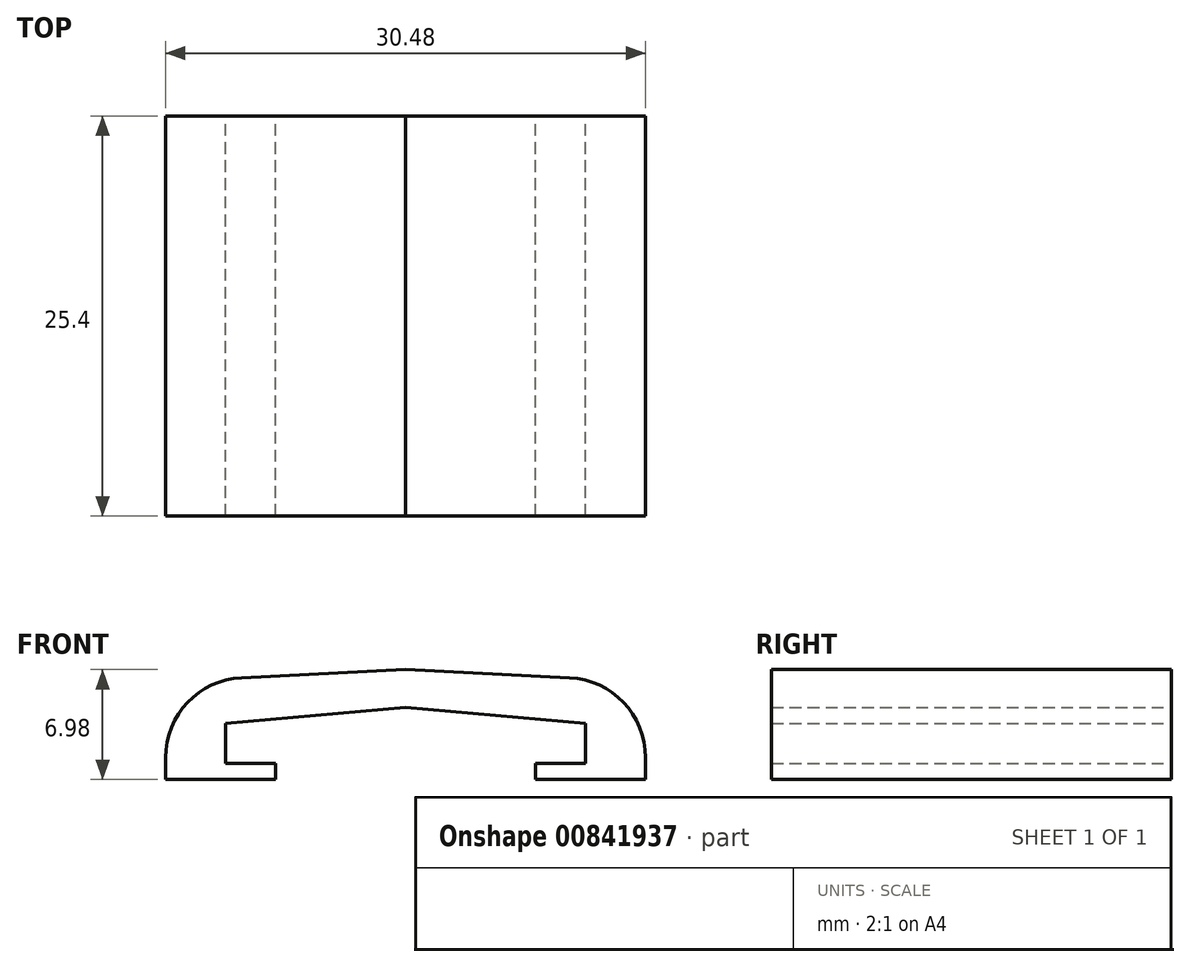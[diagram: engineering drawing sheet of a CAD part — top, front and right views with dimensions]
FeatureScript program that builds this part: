
annotation { "Feature Type Name" : "Feature", "Feature Type Description" : "" }
export const myFeature = defineFeature(function(context is Context, id is Id, definition is map)
    precondition{}
    {
        {
            var Q0;
            Q0=qCreatedBy(makeId("Front.planeOp"),FACE);
            var sketch = newSketch(context, id + "F0", { "sketchPlane" : qUnion([Q0])});
            skLineSegment(sketch, "E0", {"start": v(-11.43, 17.28) * mm, "end": v(11.43, 17.28) * mm, "construction": true});
            skLineSegment(sketch, "E1", {"start": v(-11.43, 17.28) * mm, "end": v(0, 18.28) * mm});
            skLineSegment(sketch, "E2", {"start": v(0, 18.28) * mm, "end": v(11.43, 17.28) * mm});
            skLineSegment(sketch, "E3", {"start": v(-11.43, 17.28) * mm, "end": v(-11.43, 14.74) * mm});
            skLineSegment(sketch, "E4", {"start": v(11.43, 17.28) * mm, "end": v(11.43, 14.74) * mm});
            skLineSegment(sketch, "E5", {"start": v(-11.43, 14.74) * mm, "end": v(-8.25, 14.74) * mm});
            skLineSegment(sketch, "E6.MirrorCS", {"start": v(11.43, 14.74) * mm, "end": v(8.25, 14.74) * mm});
            skLineSegment(sketch, "E7", {"start": v(-8.25, 14.74) * mm, "end": v(-8.25, 13.72) * mm});
            skLineSegment(sketch, "E8", {"start": v(-8.25, 13.72) * mm, "end": v(-15.24, 13.72) * mm});
            skLineSegment(sketch, "E9", {"start": v(-15.24, 13.72) * mm, "end": v(-15.24, 19.94) * mm});
            skLineSegment(sketch, "E10", {"start": v(-15.24, 19.94) * mm, "end": v(0, 20.7) * mm});
            skLineSegment(sketch, "E11.MirrorCS", {"start": v(15.24, 19.94) * mm, "end": v(0, 20.7) * mm});
            skLineSegment(sketch, "E12.MirrorCS", {"start": v(15.24, 13.72) * mm, "end": v(15.24, 19.94) * mm});
            skLineSegment(sketch, "E13.MirrorCS", {"start": v(8.25, 13.72) * mm, "end": v(15.24, 13.72) * mm});
            skLineSegment(sketch, "E14.MirrorCS", {"start": v(8.25, 14.74) * mm, "end": v(8.25, 13.72) * mm});
            skSolve(sketch);
        }
        {
            var Q0;
            Q0=makeQuery(id+"F0.imprint","IMPRINT",FACE,{"disambiguationData":[TD([[makeQuery(id+"F0.imprint","IMPRINT",EDGE,{"derivedFrom":sQuery(id+"F0.wireOp",EDGE,"E1")}),1.0]])]});
            extrude(context, id + "F1", {"entities" : qUnion([Q0]), "depth" : 25.4 * mm, "offsetDistance" : 25.4 * mm});
        }
        {
            var Q0;
            Q0=makeQuery(id+"F1.opExtrude","SWEPT_EDGE",EDGE,{"disambiguationData":[OSD([sQuery(id+"F0.wireOp",EDGE,"E11.MirrorCS"),sQuery(id+"F0.wireOp",EDGE,"E12.MirrorCS")])]});
            var Q1;
            Q1=makeQuery(id+"F1.opExtrude","SWEPT_EDGE",EDGE,{"disambiguationData":[OSD([sQuery(id+"F0.wireOp",EDGE,"E9"),sQuery(id+"F0.wireOp",EDGE,"E10")])]});
            fillet(context, id + "F2", {"entities" : qUnion([Q0, Q1]), "radius" : 5.08 * mm, "tangentPropagation" : true, "allowEdgeOverflow" : false});
        }
    });
